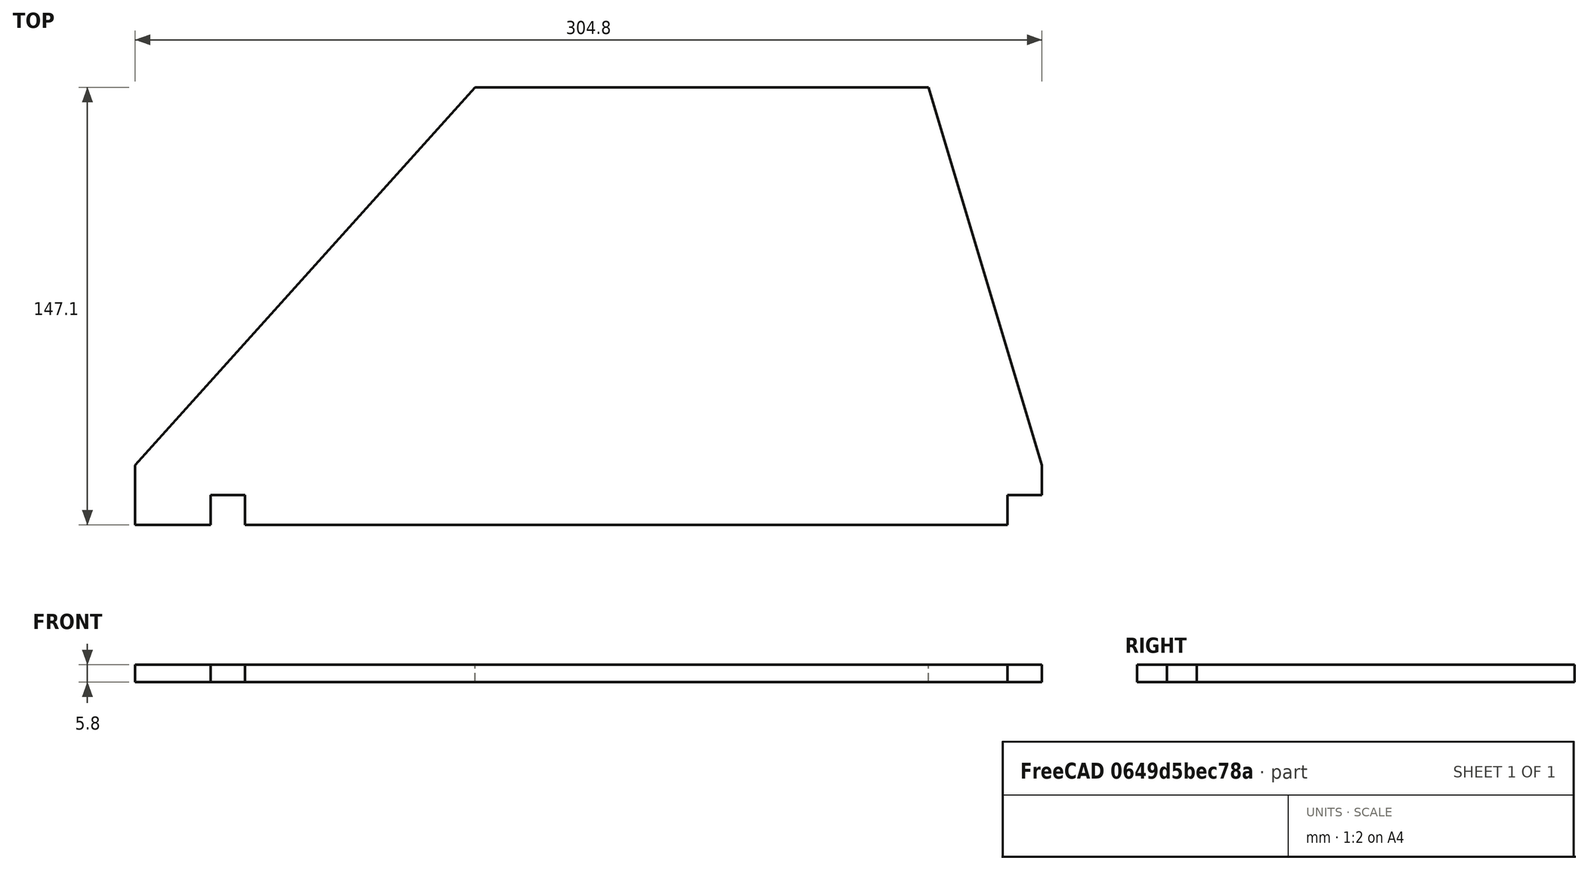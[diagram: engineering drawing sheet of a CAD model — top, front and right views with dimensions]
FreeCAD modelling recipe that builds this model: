
FCSTD DOCUMENT  (FreeCAD 1.0R39109 (Git))
Label: Fin
License: Creative Commons Attribution-ShareAlike 4.0
LicenseURL: https://creativecommons.org/licenses/by-sa/4.0/
objects: Sketcher::SketchObject×1, PartDesign::Pad×1, PartDesign::Body×1
note: 6 computed .brp shape members not serialized (recipe doc carries the construction recipe); baked Part::Feature solids carry a one-line shape summary decoded from their .brp
EXTERNAL_REF file=Variables.FCStd obj=VarSet

FEATURE [Sketcher::SketchObject] Sketch
  ArcFitTolerance = 1e-06
  AttachmentSupport = -> [XY_Plane]
  FullyConstrained = true
  MakeInternals = false
  MapMode = 5
  expr: Constraints[23] = Variables#VarSet.Fin_TabHeight
  expr: Constraints[24] = Variables#VarSet.Fin_TabHeight / 2
  expr: Constraints[26] = Variables#VarSet.CR_Thickness
  expr: Constraints[27] = Variables#VarSet.Fin_MiddleCR
  expr: Constraints[28] = Variables#VarSet.Fin_TabHeight / 2
  expr: Constraints[29] = Variables#VarSet.Fin_RootChord
  expr: Constraints[30] = Variables#VarSet.Fin_TipChord
  expr: Constraints[31] = Variables#VarSet.Fin_TabHeight / 2
  expr: Constraints[32] = Variables#VarSet.CR_Thickness
  expr: Constraints[33] = Variables#VarSet.Fin_Height
  expr: Constraints[34] = Variables#VarSet.Fin_Sweep
  sketch-geometry (12):
    g0: LineSegment StartX=0 StartY=-20.1 StartZ=0 EndX=0 EndY=0 EndZ=0
    g1: LineSegment StartX=0 StartY=0 StartZ=0 EndX=114.3 EndY=127 EndZ=0
    g2: LineSegment StartX=114.3 StartY=127 StartZ=0 EndX=266.7 EndY=127 EndZ=0
    g3: LineSegment StartX=266.7 StartY=127 StartZ=0 EndX=304.8 EndY=0 EndZ=0
    g4: LineSegment StartX=304.8 StartY=0 StartZ=0 EndX=304.8 EndY=-10.05 EndZ=0
    g5: LineSegment StartX=304.8 StartY=-10.05 StartZ=0 EndX=293.2 EndY=-10.05 EndZ=0
    g6: LineSegment StartX=293.2 StartY=-10.05 StartZ=0 EndX=293.2 EndY=-20.1 EndZ=0
    g7: LineSegment StartX=293.2 StartY=-20.1 StartZ=0 EndX=37 EndY=-20.1 EndZ=0
    g8: LineSegment StartX=37 StartY=-20.1 StartZ=0 EndX=37 EndY=-10.05 EndZ=0
    g9: LineSegment StartX=37 StartY=-10.05 StartZ=0 EndX=25.4 EndY=-10.05 EndZ=0
    g10: LineSegment StartX=25.4 StartY=-10.05 StartZ=0 EndX=25.4 EndY=-20.1 EndZ=0
    g11: LineSegment StartX=25.4 StartY=-20.1 StartZ=0 EndX=0 EndY=-20.1 EndZ=0
  constraints (35):
    c: PointOnObject(g0,g-2)
    c: Coincident(g0,g-1)
    c: Coincident(g0,g1)
    c: Coincident(g1,g2)
    c: Horizontal(g2)
    c: Coincident(g2,g3)
    c: PointOnObject(g3,g-1)
    c: Coincident(g3,g4)
    c: Vertical(g4)
    c: Coincident(g4,g5)
    c: Horizontal(g5)
    c: Coincident(g5,g6)
    c: Vertical(g6)
    c: Coincident(g6,g7)
    c: Horizontal(g7)
    c: Coincident(g7,g8)
    c: Vertical(g8)
    c: Coincident(g8,g9)
    c: Horizontal(g9)
    c: Coincident(g9,g10)
    c: Vertical(g10)
    c: Coincident(g10,g11)
    c: Coincident(g11,g0)
    c: DistanceY(g0,g0) = 20.1
    c: DistanceY(g10,g9) = 10.05
    c: Horizontal(g11)
    c: DistanceX(g9,g8) = 11.6
    c: DistanceX(g0,g10) = 25.4
    c: DistanceY(g7,g8) = 10.05
    c: DistanceX(g0,g3) = 304.8
    c: DistanceX(g1,g2) = 152.4
    c: DistanceY(g6,g5) = 10.05
    c: DistanceX(g5,g4) = 11.6
    c: DistanceY(g0,g1) = 127
    c: DistanceX(g0,g1) = 114.3
FEATURE [PartDesign::Pad] Pad
  Direction = (0,0,1)
  Length = 5.8
  Length2 = 10
  Profile = -> Sketch
  ReferenceAxis = -> Sketch [N_Axis]
  Refine = true
  Suppressed = false
  Type = 0
  expr: Length = Variables#VarSet.FinThickness
FEATURE [PartDesign::Body] Body
  AllowCompound = false
  Group = -> [Sketch,Pad]
  Origin = -> Origin
  Tip = -> Pad
